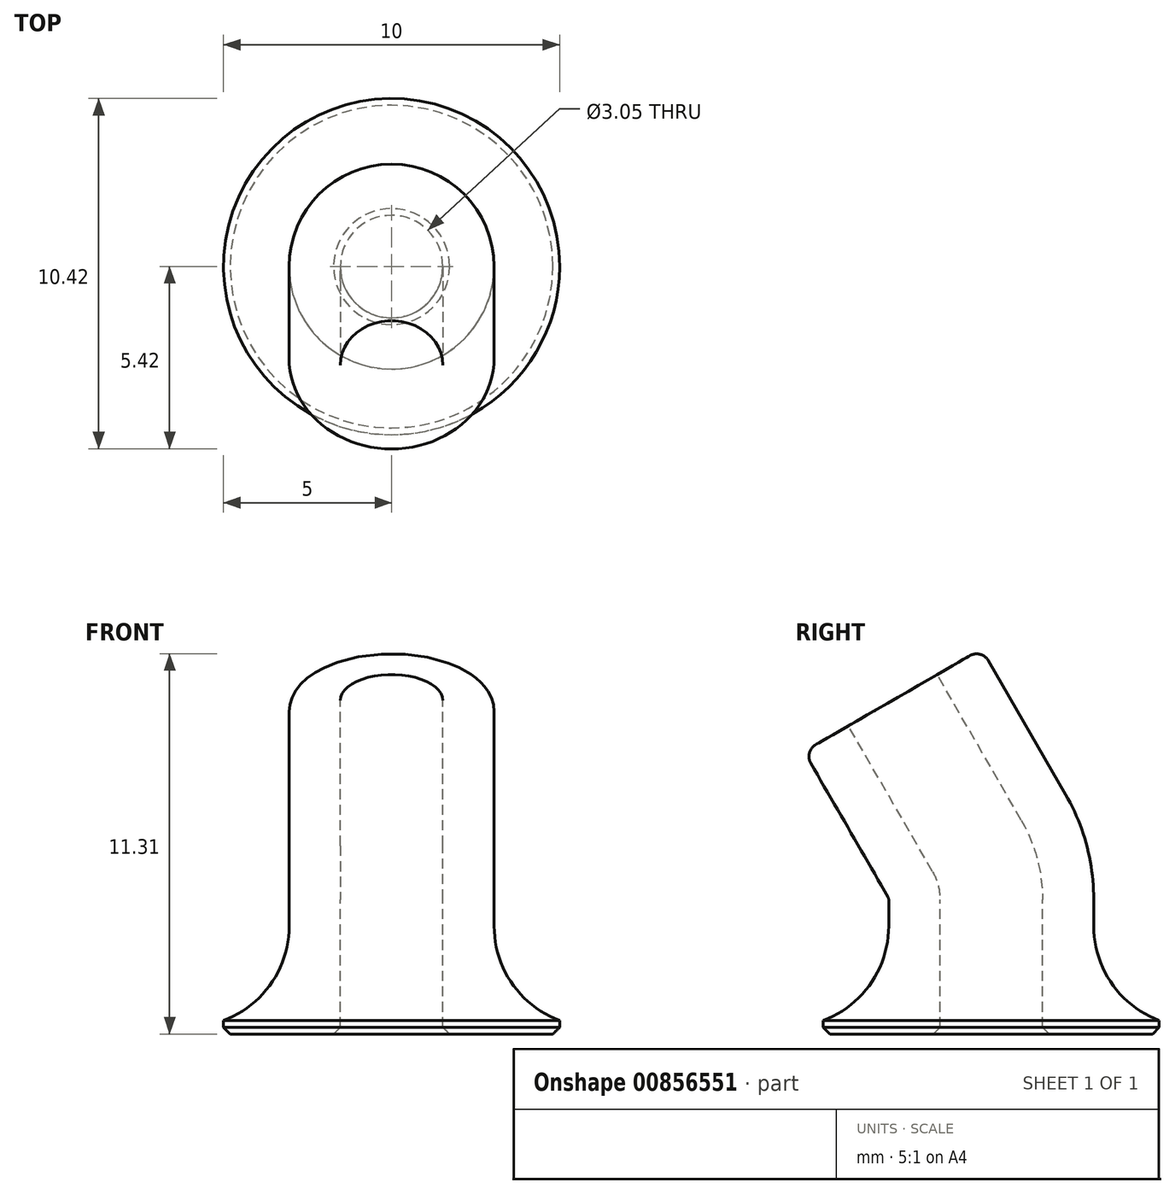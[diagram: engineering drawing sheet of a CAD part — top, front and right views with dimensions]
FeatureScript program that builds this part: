
annotation { "Feature Type Name" : "Feature", "Feature Type Description" : "" }
export const myFeature = defineFeature(function(context is Context, id is Id, definition is map)
    precondition{}
    {
        {
            var Q0;
            Q0=qCreatedBy(makeId("Top.planeOp"),FACE);
            var sketch = newSketch(context, id + "F0", { "sketchPlane" : qUnion([Q0])});
            skCircle(sketch, "E0", {"center": v(0, 0) * mm, "radius": 5 * mm});
            skCircle(sketch, "E1", {"center": v(0, 0) * mm, "radius": 3 * mm});
            skSolve(sketch);
        }
        {
            var Q0;
            Q0 = qSketchRegion(id + "F0", true);
            extrude(context, id + "F1", {"entities" : qUnion([Q0]), "depth" : 0.4 * mm, "offsetDistance" : 25 * mm});
        }
        {
            var Q0;
            Q0=qCreatedBy(makeId("Right.planeOp"),FACE);
            var sketch = newSketch(context, id + "F2", { "sketchPlane" : qUnion([Q0])});
            skLineSegment(sketch, "E2", {"start": v(0, 0) * mm, "end": v(0, 4) * mm});
            skArc(sketch, "E3", {"start": v(0, 4) * mm, "mid": v(-0.1, 4.83) * mm, "end": v(-0.43, 5.6) * mm});
            skLineSegment(sketch, "E4", {"start": v(-0.43, 5.6) * mm, "end": v(-2.93, 9.93) * mm});
            skSolve(sketch);
        }
        {
            var Q0;
            Q0=qCreatedBy(makeId("Top.planeOp"),FACE);
            var sketch = newSketch(context, id + "F3", { "sketchPlane" : qUnion([Q0])});
            skCircle(sketch, "E5", {"center": v(0, 0) * mm, "radius": 1.52 * mm});
            skCircle(sketch, "E6", {"center": v(0, 0) * mm, "radius": 3.05 * mm});
            skSolve(sketch);
        }
        {
            var Q0;
            Q0=makeQuery(id+"F3.imprint","IMPRINT",FACE,{"disambiguationData":[TD([[makeQuery(id+"F3.imprint","IMPRINT",EDGE,{"derivedFrom":sQuery(id+"F3.wireOp",EDGE,"E5")}),-1.0]])]});
            var Q1;
            Q1=sQuery(id+"F2.wireOp",EDGE,"E2");
            var Q2;
            Q2=sQuery(id+"F2.wireOp",EDGE,"E3");
            var Q3;
            Q3=sQuery(id+"F2.wireOp",EDGE,"E4");
            sweep(context, id + "F4", {"operationType" : NewBodyOperationType.ADD, "profiles" : qUnion([Q0]), "path" : qUnion([Q1, Q2, Q3])});
        }
        {
            var Q0;
            Q0=makeQuery(id+"F4.boolean.opBoolean","INTERSECT",EDGE,{"derivedFrom":[makeQuery(id+"F1.opExtrude","CAP_FACE",FACE,{"disambiguationData":[OSD([sQuery(id+"F0.wireOp",EDGE,"E0"),sQuery(id+"F0.wireOp",EDGE,"E1")])],"isStart":false}),makeQuery(id+"F4.opSweep","SWEPT_FACE",FACE,{"disambiguationData":[OSD([sQuery(id+"F2.wireOp",EDGE,"E2"),sQuery(id+"F3.wireOp",EDGE,"E6")])]})]});
            fillet(context, id + "F5", {"entities" : qUnion([Q0]), "radius" : 3 * mm, "allowEdgeOverflow" : false});
        }
        {
            var Q0;
            Q0=makeQuery(id+"F4.boolean.opBoolean","MERGE",FACE,{"derivedFrom":[makeQuery(id+"F1.opExtrude","CAP_FACE",FACE,{"disambiguationData":[OSD([sQuery(id+"F0.wireOp",EDGE,"E0"),sQuery(id+"F0.wireOp",EDGE,"E1")])],"isStart":true}),makeQuery(id+"F4.opSweep","CAP_FACE",FACE,{"disambiguationData":[OSD([sQuery(id+"F2.wireOp",VERTEX,"E2.start"),sQuery(id+"F3.wireOp",EDGE,"E5"),sQuery(id+"F3.wireOp",EDGE,"E6")])],"isStart":true})]});
            chamfer(context, id + "F6", {"entities" : qUnion([Q0]), "width" : 0.2 * mm});
        }
        {
            var Q0;
            Q0=makeQuery(id+"F4.opSweep","CAP_EDGE",EDGE,{"disambiguationData":[OSD([sQuery(id+"F2.wireOp",VERTEX,"E4.end"),sQuery(id+"F3.wireOp",EDGE,"E6")])],"isStart":false});
            fillet(context, id + "F7", {"entities" : qUnion([Q0]), "radius" : 0.4 * mm, "allowEdgeOverflow" : false});
        }
    });
